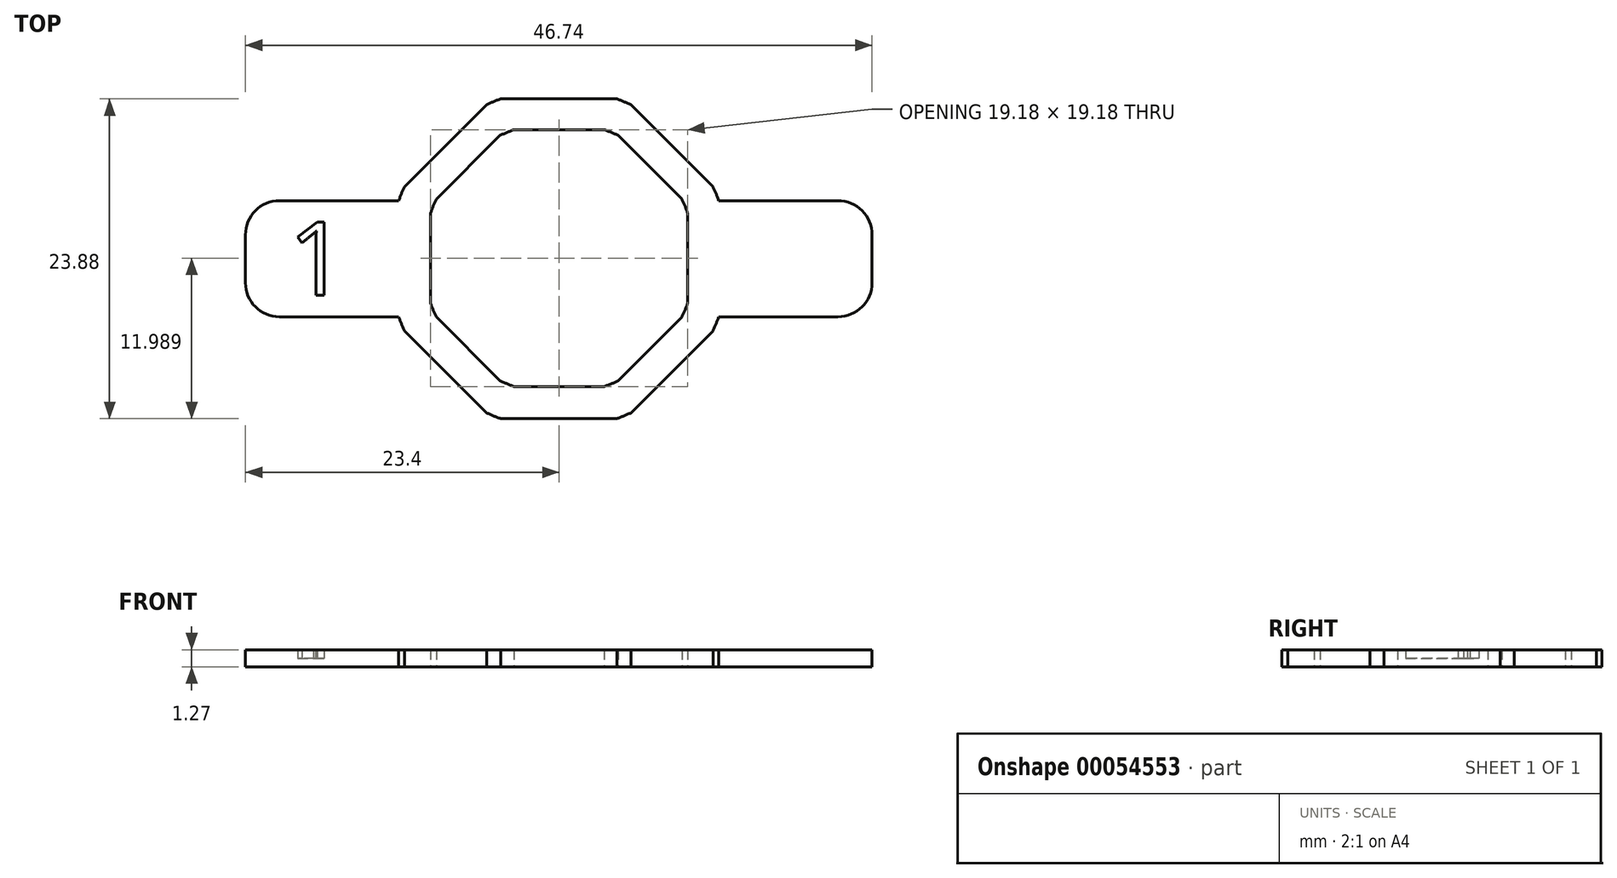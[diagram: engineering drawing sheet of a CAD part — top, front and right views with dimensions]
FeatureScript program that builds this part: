
annotation { "Feature Type Name" : "Feature", "Feature Type Description" : "" }
export const myFeature = defineFeature(function(context is Context, id is Id, definition is map)
    precondition{}
    {
        {
            var Q0;
            Q0=qCreatedBy(makeId("Top.planeOp"),FACE);
            var sketch = newSketch(context, id + "F0", { "sketchPlane" : qUnion([Q0])});
            skArc(sketch, "E0", {"start": v(-11.5, 5.38) * mm, "mid": v(-11.73, 4.86) * mm, "end": v(-11.94, 4.33) * mm});
            skLineSegment(sketch, "E1", {"start": v(-4.33, 11.94) * mm, "end": v(4.33, 11.94) * mm});
            skPoint(sketch, "E2.end.orphan", {"position": v(0, 11.94) * mm});
            skPoint(sketch, "E2.start.orphan", {"position": v(0, 12.7) * mm});
            skLineSegment(sketch, "E3.1.0", {"start": v(-11.5, 5.38) * mm, "end": v(-5.38, 11.5) * mm});
            skLineSegment(sketch, "E3.2.0", {"start": v(-11.94, -4.33) * mm, "end": v(-11.94, 4.33) * mm});
            skLineSegment(sketch, "E3.3.0", {"start": v(-5.38, -11.5) * mm, "end": v(-11.5, -5.38) * mm});
            skLineSegment(sketch, "E3.4.0", {"start": v(4.33, -11.94) * mm, "end": v(-4.33, -11.94) * mm});
            skLineSegment(sketch, "E3.5.0", {"start": v(11.5, -5.38) * mm, "end": v(5.38, -11.5) * mm});
            skLineSegment(sketch, "E3.6.0", {"start": v(11.94, 4.33) * mm, "end": v(11.94, -4.33) * mm});
            skLineSegment(sketch, "E3.7.0", {"start": v(5.38, 11.5) * mm, "end": v(11.5, 5.38) * mm});
            skArc(sketch, "E4.trimOffspring", {"start": v(-4.33, 11.94) * mm, "mid": v(-4.86, 11.73) * mm, "end": v(-5.38, 11.5) * mm});
            skArc(sketch, "E5.trimOffspring", {"start": v(5.38, 11.5) * mm, "mid": v(4.86, 11.73) * mm, "end": v(4.33, 11.94) * mm});
            skArc(sketch, "E6.trimOffspring", {"start": v(11.94, 4.33) * mm, "mid": v(11.73, 4.86) * mm, "end": v(11.5, 5.38) * mm});
            skArc(sketch, "E7.trimOffspring", {"start": v(11.5, -5.38) * mm, "mid": v(11.73, -4.86) * mm, "end": v(11.94, -4.33) * mm});
            skArc(sketch, "E8.trimOffspring", {"start": v(-5.38, -11.5) * mm, "mid": v(-4.86, -11.73) * mm, "end": v(-4.33, -11.94) * mm});
            skArc(sketch, "E9.trimOffspring", {"start": v(-11.94, -4.33) * mm, "mid": v(-11.73, -4.86) * mm, "end": v(-11.5, -5.38) * mm});
            skArc(sketch, "E10.trimOffspring", {"start": v(4.33, -11.94) * mm, "mid": v(4.86, -11.73) * mm, "end": v(5.38, -11.5) * mm});
            skLineSegment(sketch, "E11.6.0", {"start": v(9.62, 3.4) * mm, "end": v(9.62, -3.31) * mm});
            skLineSegment(sketch, "E11.4.0", {"start": v(3.39, -9.54) * mm, "end": v(-3.33, -9.54) * mm});
            skLineSegment(sketch, "E11.3.0", {"start": v(-4.37, -9.1) * mm, "end": v(-9.13, -4.36) * mm});
            skLineSegment(sketch, "E11.7.0", {"start": v(4.43, 9.2) * mm, "end": v(9.19, 4.45) * mm});
            skLineSegment(sketch, "E11.5.0", {"start": v(9.19, -4.36) * mm, "end": v(4.43, -9.1) * mm});
            skPoint(sketch, "E12.start.orphan", {"position": v(0.03, 10.2) * mm});
            skLineSegment(sketch, "E11.2.0", {"start": v(-9.56, -3.31) * mm, "end": v(-9.56, 3.4) * mm});
            skLineSegment(sketch, "E11.1.0", {"start": v(-9.13, 4.45) * mm, "end": v(-4.37, 9.2) * mm});
            skLineSegment(sketch, "E13", {"start": v(-3.33, 9.64) * mm, "end": v(3.39, 9.64) * mm});
            skPoint(sketch, "E12.end.orphan", {"position": v(0.03, 9.64) * mm});
            skPoint(sketch, "E11.center", {"position": v(0.03, 0.05) * mm});
            skArc(sketch, "E14.trimOffspring", {"start": v(3.39, -9.54) * mm, "mid": v(3.92, -9.34) * mm, "end": v(4.43, -9.1) * mm});
            skArc(sketch, "E15.trimOffspring", {"start": v(4.43, 9.2) * mm, "mid": v(3.92, 9.44) * mm, "end": v(3.39, 9.64) * mm});
            skArc(sketch, "E16.trimOffspring", {"start": v(-3.33, 9.64) * mm, "mid": v(-3.86, 9.44) * mm, "end": v(-4.37, 9.2) * mm});
            skArc(sketch, "E17", {"start": v(-9.13, 4.45) * mm, "mid": v(-9.36, 3.94) * mm, "end": v(-9.56, 3.4) * mm});
            skArc(sketch, "E18.trimOffspring", {"start": v(9.62, 3.4) * mm, "mid": v(9.42, 3.94) * mm, "end": v(9.19, 4.45) * mm});
            skArc(sketch, "E19.trimOffspring", {"start": v(-9.56, -3.31) * mm, "mid": v(-9.36, -3.84) * mm, "end": v(-9.13, -4.36) * mm});
            skArc(sketch, "E20.trimOffspring", {"start": v(-4.37, -9.1) * mm, "mid": v(-3.86, -9.34) * mm, "end": v(-3.33, -9.54) * mm});
            skArc(sketch, "E21.trimOffspring", {"start": v(9.19, -4.36) * mm, "mid": v(9.42, -3.84) * mm, "end": v(9.62, -3.31) * mm});
            skLineSegment(sketch, "E22.bottom", {"start": v(-11.94, 4.33) * mm, "end": v(-20.83, 4.33) * mm});
            skLineSegment(sketch, "E22.top", {"start": v(-11.94, -4.33) * mm, "end": v(-20.83, -4.33) * mm});
            skLineSegment(sketch, "E22.right", {"start": v(-23.37, 1.8) * mm, "end": v(-23.37, -1.8) * mm});
            skLineSegment(sketch, "E23.bottom", {"start": v(11.94, 4.33) * mm, "end": v(20.83, 4.33) * mm});
            skLineSegment(sketch, "E23.top", {"start": v(11.94, -4.33) * mm, "end": v(20.83, -4.33) * mm});
            skLineSegment(sketch, "E23.right", {"start": v(23.37, 1.8) * mm, "end": v(23.37, -1.8) * mm});
            skPoint(sketch, "E24.visualSharp", {"position": v(-23.37, 4.33) * mm});
            skArc(sketch, "E24.filletArc", {"start": v(-20.83, 4.33) * mm, "mid": v(-22.62, 3.59) * mm, "end": v(-23.37, 1.8) * mm});
            skPoint(sketch, "E25.visualSharp", {"position": v(-23.37, -4.33) * mm});
            skArc(sketch, "E25.filletArc", {"start": v(-23.37, -1.8) * mm, "mid": v(-22.62, -3.59) * mm, "end": v(-20.83, -4.33) * mm});
            skPoint(sketch, "E26.visualSharp", {"position": v(23.37, 4.33) * mm});
            skArc(sketch, "E26.filletArc", {"start": v(23.37, 1.8) * mm, "mid": v(22.62, 3.59) * mm, "end": v(20.83, 4.33) * mm});
            skPoint(sketch, "E27.visualSharp", {"position": v(23.37, -4.33) * mm});
            skArc(sketch, "E27.filletArc", {"start": v(20.83, -4.33) * mm, "mid": v(22.62, -3.59) * mm, "end": v(23.37, -1.8) * mm});
            skText(sketch, "E28", { "text": "1", "fontName": "OpenSans-Regular.ttf"});
            const initialGuessF0  = {"E28": [-0.02017, -0.00272, 1, 0, 0.0055]};
            skSetInitialGuess(sketch, initialGuessF0);
            skSolve(sketch);
        }
        {
            var Q0;
            Q0 = qSketchRegion(id + "F0", true);
            extrude(context, id + "F1", {"entities" : qUnion([Q0]), "depth" : 1.27 * mm});
        }
        {
            var Q0;
            Q0=makeQuery(id+"F0.imprint","IMPRINT",FACE,{"disambiguationData":[TD([[makeQuery(id+"F0.imprint","IMPRINT",EDGE,{"derivedFrom":sQuery(id+"F0.wireOp",EDGE,"E28.sketch_text.stroke-0")}),-1.0]])]});
            extrude(context, id + "F2", {"entities" : qUnion([Q0]), "operationType" : NewBodyOperationType.ADD, "depth" : 0.64 * mm});
        }
    });
